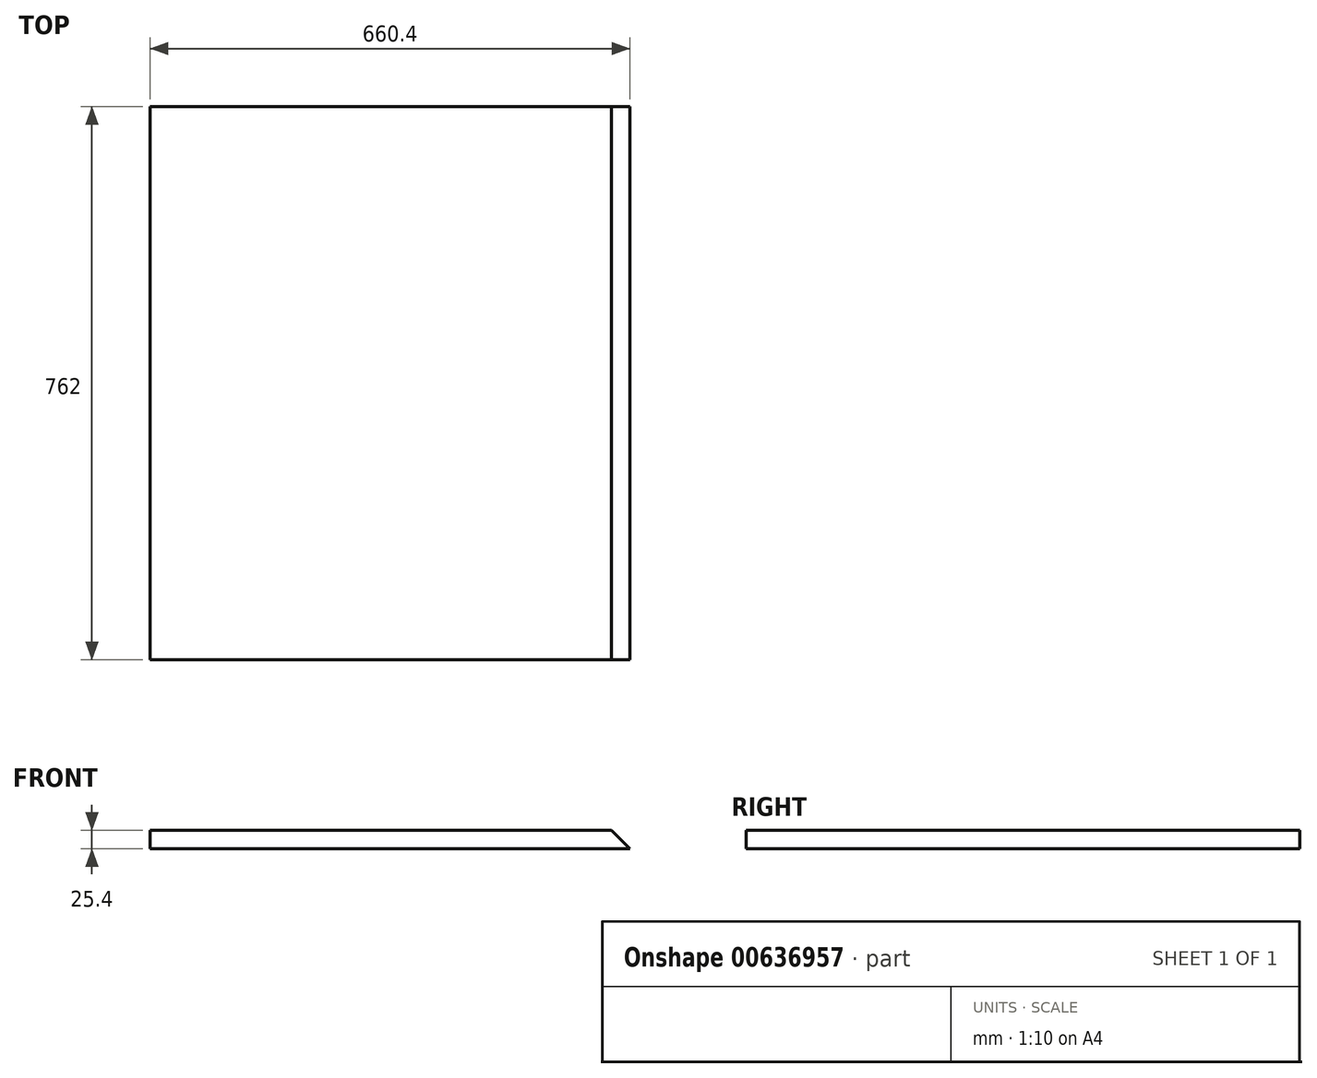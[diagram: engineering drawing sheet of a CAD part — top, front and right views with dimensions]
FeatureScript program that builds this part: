
annotation { "Feature Type Name" : "Feature", "Feature Type Description" : "" }
export const myFeature = defineFeature(function(context is Context, id is Id, definition is map)
    precondition{}
    {
        {
            var Q0;
            Q0=qCreatedBy(makeId("Top.planeOp"),FACE);
            var sketch = newSketch(context, id + "F0", { "sketchPlane" : qUnion([Q0])});
            skLineSegment(sketch, "E0.bottom", {"start": v(181.96, -603.65) * mm, "end": v(-478.44, -603.65) * mm});
            skLineSegment(sketch, "E0.top", {"start": v(181.96, 158.35) * mm, "end": v(-478.44, 158.35) * mm});
            skLineSegment(sketch, "E0.left", {"start": v(181.96, -603.65) * mm, "end": v(181.96, 158.35) * mm});
            skLineSegment(sketch, "E0.right", {"start": v(-478.44, -603.65) * mm, "end": v(-478.44, 158.35) * mm});
            skPoint(sketch, "E0.middle", {"position": v(-148.24, -222.65) * mm});
            skSolve(sketch);
        }
        {
            var Q0;
            Q0 = qSketchRegion(id + "F0", true);
            extrude(context, id + "F1", {"entities" : qUnion([Q0]), "depth" : 25.4 * mm, "offsetDistance" : 25.4 * mm});
        }
        {
            var Q0;
            Q0=makeQuery(id+"F1.opExtrude","CAP_EDGE",EDGE,{"disambiguationData":[OSD([sQuery(id+"F0.wireOp",EDGE,"E0.left")])],"isStart":false});
            chamfer(context, id + "F2", {"entities" : qUnion([Q0]), "width" : 25.4 * mm, "tangentPropagation" : true});
        }
    });
